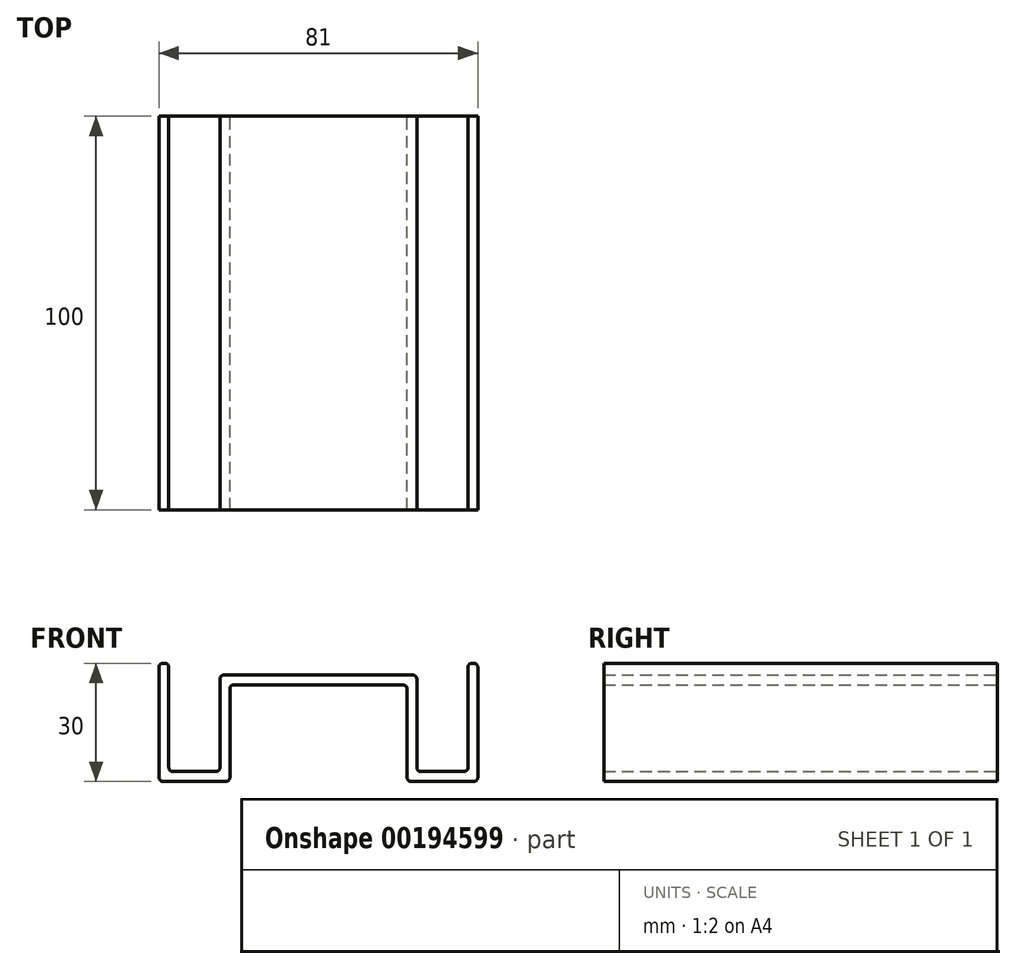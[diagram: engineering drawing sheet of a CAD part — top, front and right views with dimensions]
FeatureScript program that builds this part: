
annotation { "Feature Type Name" : "Feature", "Feature Type Description" : "" }
export const myFeature = defineFeature(function(context is Context, id is Id, definition is map)
    precondition{}
    {
        {
            var Q0;
            Q0=qCreatedBy(makeId("Front.planeOp"),FACE);
            var sketch = newSketch(context, id + "F0", { "sketchPlane" : qUnion([Q0])});
            skLineSegment(sketch, "E0.bottom", {"start": v(39.5, -15) * mm, "end": v(23.5, -15) * mm});
            skLineSegment(sketch, "E0.top", {"start": v(39.5, 15) * mm, "end": v(39, 15) * mm});
            skLineSegment(sketch, "E0.left", {"start": v(40.5, -14) * mm, "end": v(40.5, 14) * mm});
            skLineSegment(sketch, "E0.right", {"start": v(-40.5, -14) * mm, "end": v(-40.5, 14) * mm});
            skPoint(sketch, "E0.middle", {"position": v(0, 0) * mm});
            skLineSegment(sketch, "E1", {"start": v(-21.5, 9.5) * mm, "end": v(21.5, 9.5) * mm});
            skLineSegment(sketch, "E2", {"start": v(-24, 12) * mm, "end": v(24, 12) * mm});
            skLineSegment(sketch, "E3", {"start": v(38, 14) * mm, "end": v(38, -11.5) * mm});
            skLineSegment(sketch, "E4", {"start": v(37, -12.5) * mm, "end": v(26, -12.5) * mm});
            skLineSegment(sketch, "E5", {"start": v(25, -11.5) * mm, "end": v(25, 9.5) * mm});
            skLineSegment(sketch, "E6", {"start": v(22.5, -14) * mm, "end": v(22.5, 8.5) * mm});
            skLineSegment(sketch, "E7", {"start": v(-38, 14) * mm, "end": v(-38, 12) * mm});
            skLineSegment(sketch, "E8", {"start": v(-37, -12.5) * mm, "end": v(-26, -12.5) * mm});
            skLineSegment(sketch, "E9", {"start": v(-25, -11.5) * mm, "end": v(-25, 9.5) * mm});
            skLineSegment(sketch, "E10", {"start": v(-22.5, 8.5) * mm, "end": v(-22.5, -14) * mm});
            skLineSegment(sketch, "E11.trimOffspring", {"start": v(-38, 9.5) * mm, "end": v(-38, -11.5) * mm});
            skLineSegment(sketch, "E12", {"start": v(-38, 12) * mm, "end": v(-38, 9.5) * mm});
            skLineSegment(sketch, "E13.trimOffspring", {"start": v(-39, 15) * mm, "end": v(-39.5, 15) * mm});
            skLineSegment(sketch, "E14", {"start": v(-25, 9.5) * mm, "end": v(-25, 11) * mm});
            skLineSegment(sketch, "E15.trimOffspring", {"start": v(-23.5, -15) * mm, "end": v(-39.5, -15) * mm});
            skLineSegment(sketch, "E16", {"start": v(25, 9.5) * mm, "end": v(25, 11) * mm});
            skPoint(sketch, "E17.visualSharp", {"position": v(-38, -12.5) * mm});
            skArc(sketch, "E17.filletArc", {"start": v(-38, -11.5) * mm, "mid": v(-37.7, -12.2) * mm, "end": v(-37, -12.5) * mm});
            skPoint(sketch, "E18.visualSharp", {"position": v(-25, -12.5) * mm});
            skArc(sketch, "E18.filletArc", {"start": v(-26, -12.5) * mm, "mid": v(-25.3, -12.2) * mm, "end": v(-25, -11.5) * mm});
            skPoint(sketch, "E19.visualSharp", {"position": v(-25, 12) * mm});
            skArc(sketch, "E19.filletArc", {"start": v(-24, 12) * mm, "mid": v(-24.7, 11.7) * mm, "end": v(-25, 11) * mm});
            skPoint(sketch, "E20.visualSharp", {"position": v(-38, 15) * mm});
            skArc(sketch, "E20.filletArc", {"start": v(-38, 14) * mm, "mid": v(-38.3, 14.7) * mm, "end": v(-39, 15) * mm});
            skPoint(sketch, "E21.visualSharp", {"position": v(-40.5, 15) * mm});
            skArc(sketch, "E21.filletArc", {"start": v(-39.5, 15) * mm, "mid": v(-40.2, 14.7) * mm, "end": v(-40.5, 14) * mm});
            skPoint(sketch, "E22.visualSharp", {"position": v(-40.5, -15) * mm});
            skArc(sketch, "E22.filletArc", {"start": v(-40.5, -14) * mm, "mid": v(-40.2, -14.7) * mm, "end": v(-39.5, -15) * mm});
            skPoint(sketch, "E23.visualSharp", {"position": v(-22.5, -15) * mm});
            skArc(sketch, "E23.filletArc", {"start": v(-23.5, -15) * mm, "mid": v(-22.8, -14.7) * mm, "end": v(-22.5, -14) * mm});
            skPoint(sketch, "E24.visualSharp", {"position": v(-22.5, 9.5) * mm});
            skArc(sketch, "E24.filletArc", {"start": v(-21.5, 9.5) * mm, "mid": v(-22.2, 9.2) * mm, "end": v(-22.5, 8.5) * mm});
            skPoint(sketch, "E25.visualSharp", {"position": v(25, 12) * mm});
            skArc(sketch, "E25.filletArc", {"start": v(25, 11) * mm, "mid": v(24.7, 11.7) * mm, "end": v(24, 12) * mm});
            skPoint(sketch, "E26.visualSharp", {"position": v(25, -12.5) * mm});
            skArc(sketch, "E26.filletArc", {"start": v(25, -11.5) * mm, "mid": v(25.3, -12.2) * mm, "end": v(26, -12.5) * mm});
            skPoint(sketch, "E27.visualSharp", {"position": v(38, -12.5) * mm});
            skArc(sketch, "E27.filletArc", {"start": v(37, -12.5) * mm, "mid": v(37.7, -12.2) * mm, "end": v(38, -11.5) * mm});
            skPoint(sketch, "E28.visualSharp", {"position": v(38, 15) * mm});
            skArc(sketch, "E28.filletArc", {"start": v(39, 15) * mm, "mid": v(38.3, 14.7) * mm, "end": v(38, 14) * mm});
            skPoint(sketch, "E29.visualSharp", {"position": v(40.5, 15) * mm});
            skArc(sketch, "E29.filletArc", {"start": v(40.5, 14) * mm, "mid": v(40.2, 14.7) * mm, "end": v(39.5, 15) * mm});
            skPoint(sketch, "E30.visualSharp", {"position": v(40.5, -15) * mm});
            skArc(sketch, "E30.filletArc", {"start": v(39.5, -15) * mm, "mid": v(40.2, -14.7) * mm, "end": v(40.5, -14) * mm});
            skPoint(sketch, "E31.visualSharp", {"position": v(22.5, -15) * mm});
            skArc(sketch, "E31.filletArc", {"start": v(22.5, -14) * mm, "mid": v(22.8, -14.7) * mm, "end": v(23.5, -15) * mm});
            skPoint(sketch, "E32.visualSharp", {"position": v(22.5, 9.5) * mm});
            skArc(sketch, "E32.filletArc", {"start": v(22.5, 8.5) * mm, "mid": v(22.2, 9.2) * mm, "end": v(21.5, 9.5) * mm});
            skSolve(sketch);
        }
        {
            var Q0;
            Q0=makeQuery(id+"F0.imprint","IMPRINT",FACE,{"disambiguationData":[TD([[makeQuery(id+"F0.imprint","IMPRINT",EDGE,{"derivedFrom":sQuery(id+"F0.wireOp",EDGE,"E0.bottom")}),-1.0]])]});
            extrude(context, id + "F1", {"entities" : qUnion([Q0]), "depth" : 100 * mm});
        }
    });
